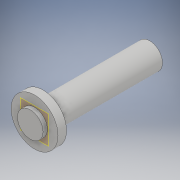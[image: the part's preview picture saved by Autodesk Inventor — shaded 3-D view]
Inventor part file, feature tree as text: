
AUTODESK INVENTOR PART (.ipt)
format: ipt  version: 2018 (Build 220112000, 112)  size: 107,008 bytes
history: native  units: in
note: dims shown in document units (in); Inventor stores cm internally (conversion verified against a paired STEP export)
features: extrude x2, sketch x2, plane x1
ambient origin geometry x8: Origin, YZ Plane, XZ Plane, XY Plane, X Axis, Y Axis, Z Axis, Center Point
bodies: Solid1 (feature_tree)
feature tree (5):
  extrude  "Extrusion1"  Depth=14.0in TaperAngle=0.0deg
  plane  "Work Plane1"
  extrude  "Extrusion2"  Depth=1.0in
  sketch  "Sketch1"  dims[d0=3.0in d1=14.0in d2=0.0in]
  sketch  "Sketch2"  dims[d3=-0.5in d4=5.5in d5=1.0in d6=0.0in]
